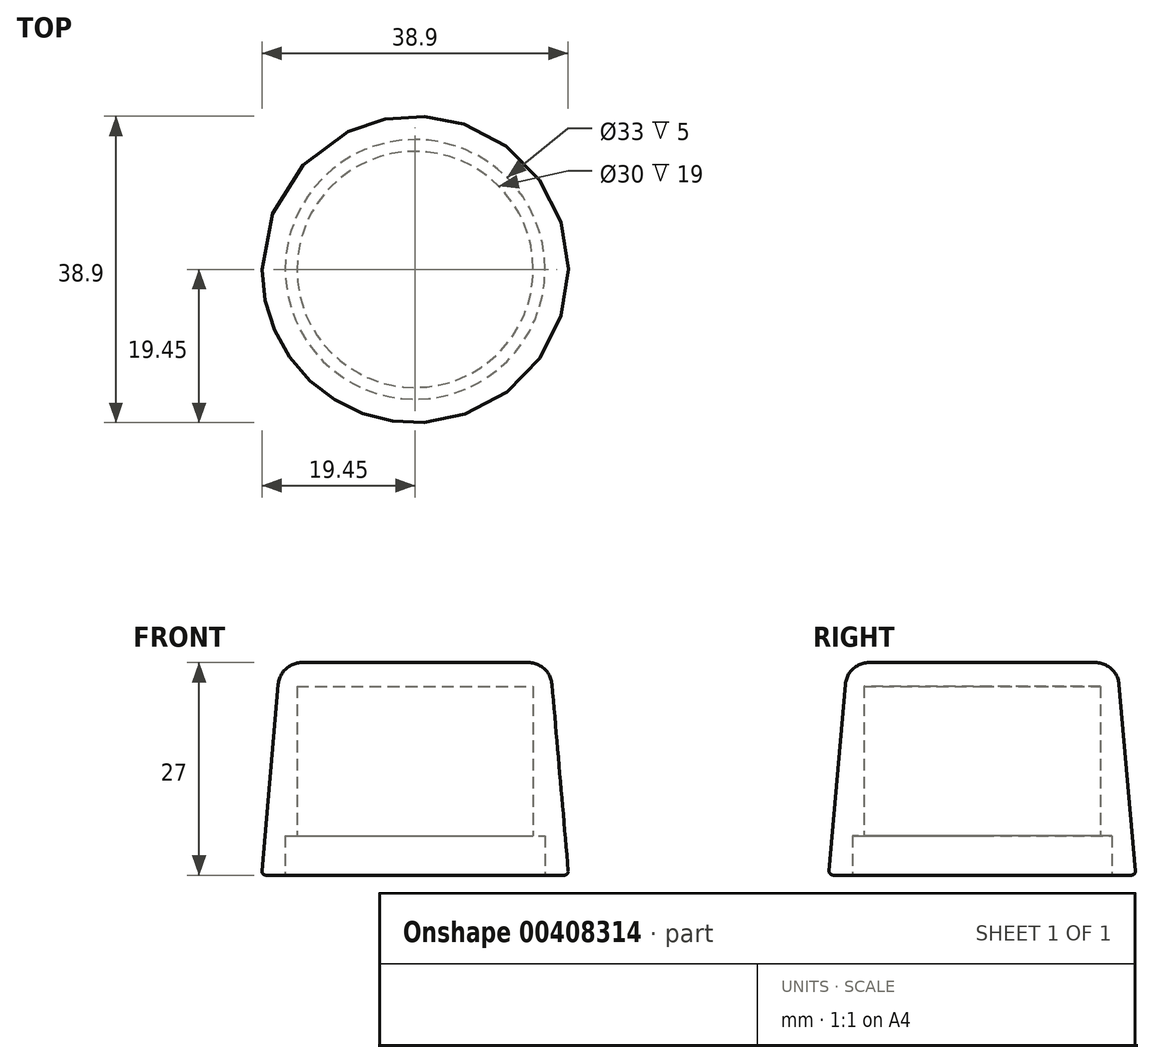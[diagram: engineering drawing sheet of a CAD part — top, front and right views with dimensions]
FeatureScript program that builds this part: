
annotation { "Feature Type Name" : "Feature", "Feature Type Description" : "" }
export const myFeature = defineFeature(function(context is Context, id is Id, definition is map)
    precondition{}
    {
        {
            var Q0;
            Q0=qCreatedBy(makeId("Front.planeOp"),FACE);
            var sketch = newSketch(context, id + "F0", { "sketchPlane" : qUnion([Q0])});
            skLineSegment(sketch, "E0", {"start": v(-19.5, 0) * mm, "end": v(-17.14, 27) * mm});
            skLineSegment(sketch, "E1", {"start": v(-17.14, 27) * mm, "end": v(0, 27) * mm});
            skPoint(sketch, "E2.visualSharp", {"position": v(-17.14, 27) * mm});
            skLineSegment(sketch, "E3", {"start": v(0, 27) * mm, "end": v(0, 24) * mm});
            skLineSegment(sketch, "E4", {"start": v(0, 24) * mm, "end": v(-15, 24) * mm});
            skLineSegment(sketch, "E5", {"start": v(-15, 24) * mm, "end": v(-15, 5) * mm});
            skLineSegment(sketch, "E6", {"start": v(-16.5, 0) * mm, "end": v(-19.5, 0) * mm});
            skLineSegment(sketch, "E7", {"start": v(0, 0) * mm, "end": v(0, 39.47) * mm, "construction": true});
            skLineSegment(sketch, "E8.top", {"start": v(-15, 5) * mm, "end": v(-16.5, 5) * mm});
            skLineSegment(sketch, "E8.right", {"start": v(-16.5, 0) * mm, "end": v(-16.5, 5) * mm});
            skSolve(sketch);
        }
        {
            var Q0;
            Q0=makeQuery(id+"F0.imprint","IMPRINT",FACE,{"disambiguationData":[TD([[makeQuery(id+"F0.imprint","IMPRINT",EDGE,{"derivedFrom":sQuery(id+"F0.wireOp",EDGE,"E0")}),-1.0]])]});
            var Q1;
            Q1=sQuery(id+"F0.wireOp",EDGE,"E1");
            var Q2;
            Q2=sQuery(id+"F0.wireOp",EDGE,"E6");
            var Q3;
            Q3=sQuery(id+"F0.wireOp",EDGE,"E5");
            var Q4;
            Q4=sQuery(id+"F0.wireOp",EDGE,"E0");
            var Q5;
            Q5=sQuery(id+"F0.wireOp",EDGE,"E4");
            var Q6;
            Q6=sQuery(id+"F0.wireOp",EDGE,"E3");
            var Q7;
            Q7=sQuery(id+"F0.wireOp",EDGE,"E2.filletArc");
            var Q8;
            Q8=sQuery(id+"F0.wireOp",EDGE,"E7");
            revolve(context, id + "F1", {"entities" : qUnion([Q0]), "surfaceEntities" : qUnion([Q1, Q2, Q3, Q4, Q5, Q6, Q7]), "axis" : qUnion([Q8]), "revolveType" : RevolveType.FULL});
        }
        {
            var Q0;
            Q0=makeQuery(id+"F1.opRevolve","SWEPT_EDGE",EDGE,{"disambiguationData":[OSD([sQuery(id+"F0.wireOp",EDGE,"E0"),sQuery(id+"F0.wireOp",EDGE,"E1")])]});
            fillet(context, id + "F2", {"entities" : qUnion([Q0]), "radius" : 3 * mm, "tangentPropagation" : true, "allowEdgeOverflow" : false});
        }
        {
            var Q0;
            Q0=makeQuery(id+"F1.opRevolve","SWEPT_EDGE",EDGE,{"disambiguationData":[OSD([sQuery(id+"F0.wireOp",EDGE,"E0"),sQuery(id+"F0.wireOp",EDGE,"E6")])]});
            fillet(context, id + "F3", {"entities" : qUnion([Q0]), "radius" : .5 * mm, "tangentPropagation" : true, "allowEdgeOverflow" : false});
        }
    });
